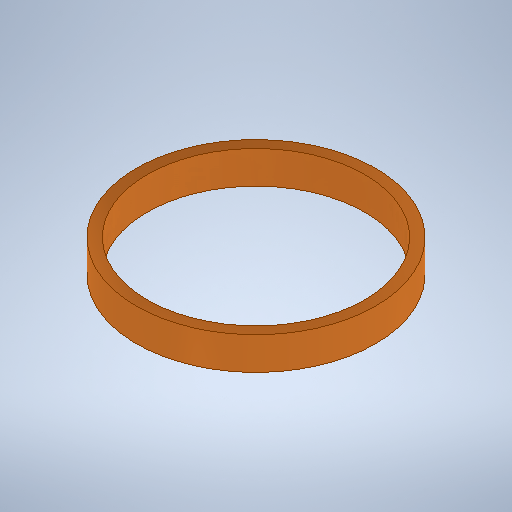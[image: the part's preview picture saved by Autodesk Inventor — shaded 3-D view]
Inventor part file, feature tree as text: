
AUTODESK INVENTOR PART (.ipt)
format: ipt  version: 2025.1 (Build 291241000, 241)  size: 248,320 bytes
history: native  units: mm
features: extrude x1, sketch x1
ambient origin geometry x8: Origin, YZ Plane, XZ Plane, XY Plane, X Axis, Y Axis, Z Axis, Center Point
bodies: Solid1 (feature_tree)
feature tree (2):
  extrude  "Extrusion1"  Depth=3.0mm
  sketch  "Sketch1"  dims[d0=22.0mm d1=20.0mm d2=3.0mm d3=0.0mm]
